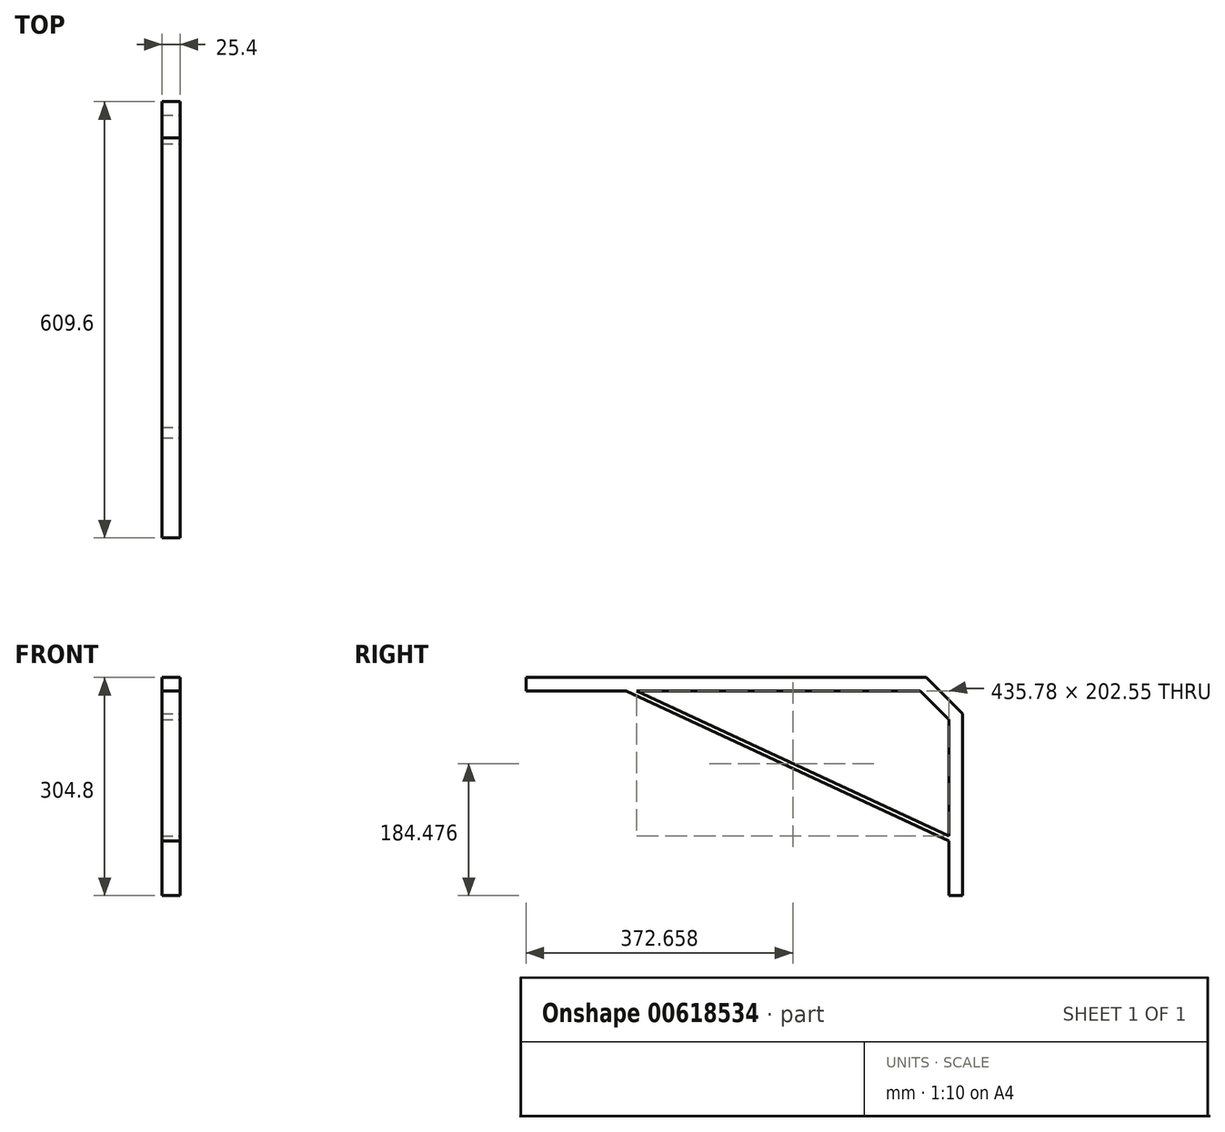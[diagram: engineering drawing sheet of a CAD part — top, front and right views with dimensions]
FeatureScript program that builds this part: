
annotation { "Feature Type Name" : "Feature", "Feature Type Description" : "" }
export const myFeature = defineFeature(function(context is Context, id is Id, definition is map)
    precondition{}
    {
        {
            var Q0;
            Q0=qCreatedBy(makeId("Right.planeOp"),FACE);
            var sketch = newSketch(context, id + "F0", { "sketchPlane" : qUnion([Q0])});
            skLineSegment(sketch, "E0", {"start": v(-50.8, 0) * mm, "end": v(0, -50.8) * mm});
            skLineSegment(sketch, "E1", {"start": v(0, -50.8) * mm, "end": v(0, -304.8) * mm});
            skLineSegment(sketch, "E2", {"start": v(-50.8, 0) * mm, "end": v(-609.6, 0) * mm});
            skPoint(sketch, "E3", {"position": v(-330.2, 0) * mm});
            skLineSegment(sketch, "E4.0", {"start": v(-19.05, -58.7) * mm, "end": v(-19.05, -304.8) * mm});
            skLineSegment(sketch, "E4.1", {"start": v(-58.7, -19.05) * mm, "end": v(-19.05, -58.7) * mm});
            skLineSegment(sketch, "E4.2", {"start": v(-58.7, -19.05) * mm, "end": v(-609.6, -19.05) * mm});
            skLineSegment(sketch, "E5", {"start": v(-609.6, 0) * mm, "end": v(-609.6, -19.05) * mm});
            skLineSegment(sketch, "E6", {"start": v(-19.05, -304.8) * mm, "end": v(0, -304.8) * mm});
            skLineSegment(sketch, "E7", {"start": v(-469.9, -19.05) * mm, "end": v(-19.05, -228.6) * mm});
            skLineSegment(sketch, "E8.0", {"start": v(-454.83, -19.05) * mm, "end": v(-19.05, -221.6) * mm});
            skSolve(sketch);
        }
        {
            var Q0;
            Q0 = qSketchRegion(id + "F0", true);
            extrude(context, id + "F1", {"entities" : qUnion([Q0]), "oppositeDirection" : true, "depth" : 25.4 * mm, "offsetDistance" : 25.4 * mm});
        }
    });
